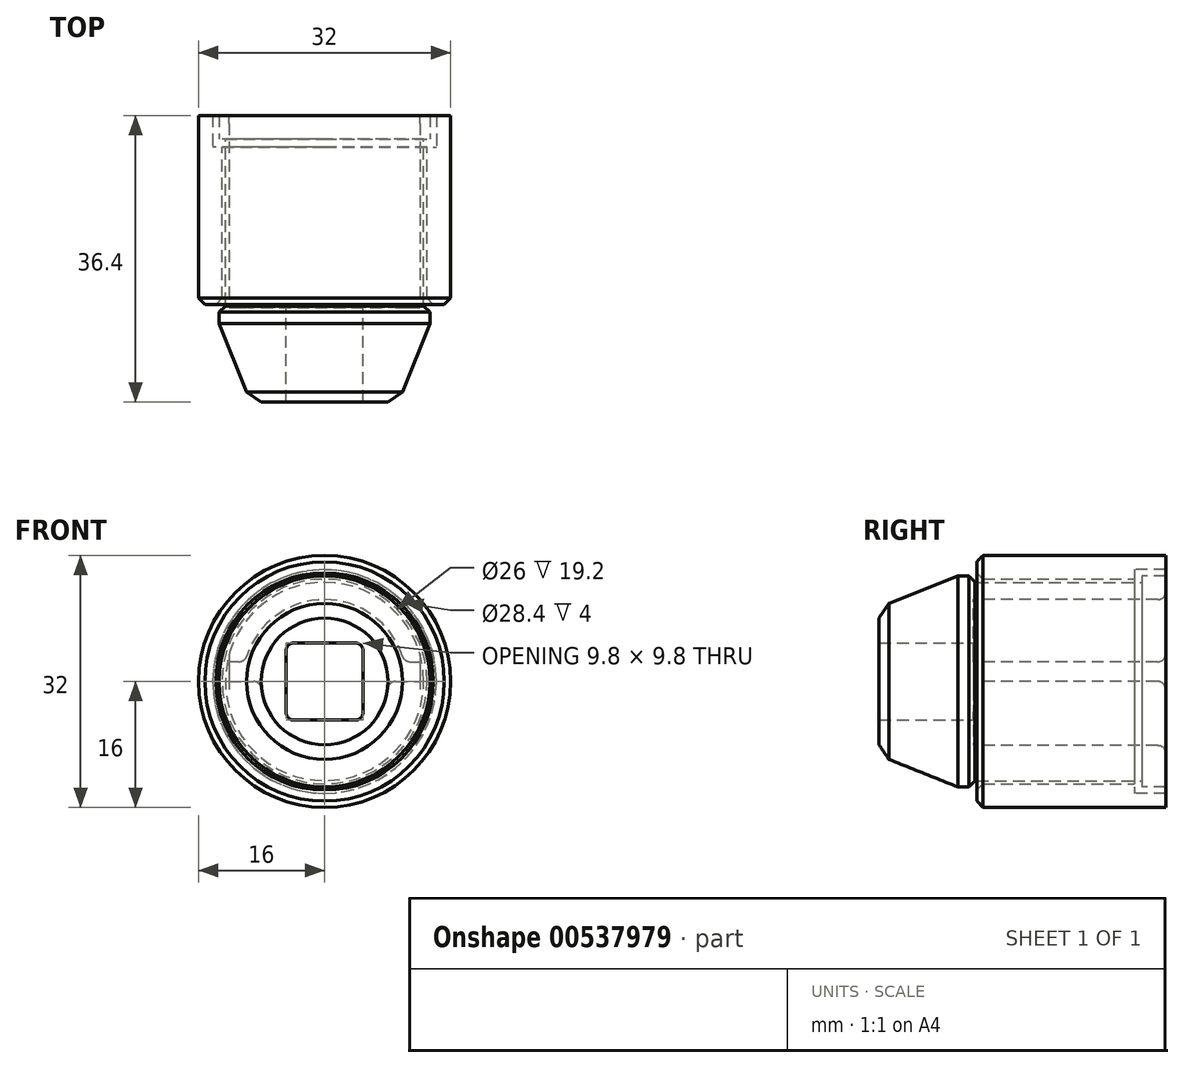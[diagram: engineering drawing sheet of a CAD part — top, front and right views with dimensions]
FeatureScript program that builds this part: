
annotation { "Feature Type Name" : "Feature", "Feature Type Description" : "" }
export const myFeature = defineFeature(function(context is Context, id is Id, definition is map)
    precondition{}
    {
        {
            var Q0;
            Q0=qCreatedBy(makeId("Front.planeOp"),FACE);
            var sketch = newSketch(context, id + "F0", { "sketchPlane" : qUnion([Q0])});
            skCircle(sketch, "E0", {"center": v(0, 0) * mm, "radius": 10.4 * mm});
            skCircle(sketch, "E1", {"center": v(0, 0) * mm, "radius": 13.4 * mm});
            skLineSegment(sketch, "E2", {"start": v(-13.4, 0) * mm, "end": v(13.4, 0) * mm});
            skCircle(sketch, "E3", {"center": v(0, 0) * mm, "radius": 8.1 * mm});
            skLineSegment(sketch, "E4.bottom", {"start": v(4.9, 4.9) * mm, "end": v(-4.9, 4.9) * mm});
            skLineSegment(sketch, "E4.top", {"start": v(4.9, -4.9) * mm, "end": v(-4.9, -4.9) * mm});
            skLineSegment(sketch, "E4.left", {"start": v(4.9, 4.9) * mm, "end": v(4.9, -4.9) * mm});
            skLineSegment(sketch, "E4.right", {"start": v(-4.9, 4.9) * mm, "end": v(-4.9, -4.9) * mm});
            skLineSegment(sketch, "E5", {"start": v(-10.1, 2.5) * mm, "end": v(-12.1, 2.5) * mm});
            skLineSegment(sketch, "E6", {"start": v(-12.1, 2.5) * mm, "end": v(-12.1, -2.5) * mm});
            skLineSegment(sketch, "E7", {"start": v(-12.1, -2.5) * mm, "end": v(-10.1, -2.5) * mm});
            skLineSegment(sketch, "E8.MirrorCS", {"start": v(10.1, 2.5) * mm, "end": v(12.1, 2.5) * mm});
            skLineSegment(sketch, "E9.MirrorCS", {"start": v(12.1, 2.5) * mm, "end": v(12.1, -2.5) * mm});
            skLineSegment(sketch, "E10.MirrorCS", {"start": v(12.1, -2.5) * mm, "end": v(10.1, -2.5) * mm});
            skSolve(sketch);
        }
        {
            var Q0;
            {var subQ5=sQuery(id+"F0.wireOp",EDGE,"E7");Q0=makeQuery(id+"F0.imprint","IMPRINT",FACE,{"disambiguationData":[TD([[makeQuery(id+"F0.imprint","IMPRINT",EDGE,{"derivedFrom":subQ5}),-1.0]])]});}
            var Q1;
            {var subQ9=sQuery(id+"F0.wireOp",EDGE,"E5");Q1=makeQuery(id+"F0.imprint","IMPRINT",FACE,{"disambiguationData":[TD([[makeQuery(id+"F0.imprint","IMPRINT",EDGE,{"derivedFrom":subQ9}),-1.0]])]});}
            extrude(context, id + "F1", {"entities" : qUnion([Q0, Q1]), "oppositeDirection" : true, "depth" : 24.4 * mm, "offsetDistance" : 25 * mm});
        }
        {
            var Q0;
            {var subQ0=sQuery(id+"F0.wireOp",EDGE,"E4.bottom");Q0=makeQuery(id+"F0.imprint","IMPRINT",FACE,{"disambiguationData":[TD([[makeQuery(id+"F0.imprint","IMPRINT",EDGE,{"derivedFrom":subQ0}),-1.0]])]});}
            var Q1;
            {var subQ0=sQuery(id+"F0.wireOp",EDGE,"E0");var subQ4=makeQuery(id+"F0.imprint","INTERSECT",VERTEX,{"derivedFrom":[subQ0,sQuery(id+"F0.wireOp",EDGE,"E8.MirrorCS")]});Q1=makeQuery(id+"F0.imprint","IMPRINT",FACE,{"disambiguationData":[TD([[makeQuery(id+"F0.imprint","IMPRINT",EDGE,{"disambiguationData":[TD([[subQ4,1.0]])],"derivedFrom":subQ0}),1.0]])]});}
            var Q2;
            {var subQ9=sQuery(id+"F0.wireOp",EDGE,"E5");Q2=makeQuery(id+"F0.imprint","IMPRINT",FACE,{"disambiguationData":[TD([[makeQuery(id+"F0.imprint","IMPRINT",EDGE,{"derivedFrom":subQ9}),-1.0]])]});}
            var Q3;
            {var subQ0=sQuery(id+"F0.wireOp",EDGE,"E4.top");Q3=makeQuery(id+"F0.imprint","IMPRINT",FACE,{"disambiguationData":[TD([[makeQuery(id+"F0.imprint","IMPRINT",EDGE,{"derivedFrom":subQ0}),1.0]])]});}
            var Q4;
            {var subQ1=sQuery(id+"F0.wireOp",EDGE,"E0");var subQ7=makeQuery(id+"F0.imprint","INTERSECT",VERTEX,{"derivedFrom":[subQ1,sQuery(id+"F0.wireOp",EDGE,"E7")]});Q4=makeQuery(id+"F0.imprint","IMPRINT",FACE,{"disambiguationData":[TD([[makeQuery(id+"F0.imprint","IMPRINT",EDGE,{"disambiguationData":[TD([[subQ7,1.0]])],"derivedFrom":subQ1}),1.0]])]});}
            var Q5;
            {var subQ5=sQuery(id+"F0.wireOp",EDGE,"E7");Q5=makeQuery(id+"F0.imprint","IMPRINT",FACE,{"disambiguationData":[TD([[makeQuery(id+"F0.imprint","IMPRINT",EDGE,{"derivedFrom":subQ5}),-1.0]])]});}
            var Q6;
            {var subQ0=sQuery(id+"F0.wireOp",EDGE,"E10.MirrorCS");Q6=makeQuery(id+"F0.imprint","IMPRINT",FACE,{"disambiguationData":[TD([[makeQuery(id+"F0.imprint","IMPRINT",EDGE,{"derivedFrom":subQ0}),-1.0]])]});}
            var Q7;
            {var subQ0=sQuery(id+"F0.wireOp",EDGE,"E8.MirrorCS");Q7=makeQuery(id+"F0.imprint","IMPRINT",FACE,{"disambiguationData":[TD([[makeQuery(id+"F0.imprint","IMPRINT",EDGE,{"derivedFrom":subQ0}),-1.0]])]});}
            var Q8;
            {var subQ0=sQuery(id+"F0.wireOp",EDGE,"E7");Q8=makeQuery(id+"F0.imprint","IMPRINT",FACE,{"disambiguationData":[TD([[makeQuery(id+"F0.imprint","IMPRINT",EDGE,{"derivedFrom":subQ0}),1.0]])]});}
            var Q9;
            {var subQ0=sQuery(id+"F0.wireOp",EDGE,"E5");Q9=makeQuery(id+"F0.imprint","IMPRINT",FACE,{"disambiguationData":[TD([[makeQuery(id+"F0.imprint","IMPRINT",EDGE,{"derivedFrom":subQ0}),1.0]])]});}
            extrude(context, id + "F2", {"entities" : qUnion([Q0, Q1, Q2, Q3, Q4, Q5, Q6, Q7, Q8, Q9]), "operationType" : NewBodyOperationType.ADD, "depth" : 12 * mm, "offsetDistance" : 25 * mm});
        }
        {
            var Q0;
            Q0=makeQuery(id+"F2.opExtrude","SWEPT_EDGE",EDGE,{"disambiguationData":[OSD([sQuery(id+"F0.wireOp",EDGE,"E4.bottom"),sQuery(id+"F0.wireOp",EDGE,"E4.right")])]});
            var Q1;
            Q1=makeQuery(id+"F2.opExtrude","SWEPT_EDGE",EDGE,{"disambiguationData":[OSD([sQuery(id+"F0.wireOp",EDGE,"E4.bottom"),sQuery(id+"F0.wireOp",EDGE,"E4.left")])]});
            var Q2;
            Q2=makeQuery(id+"F2.opExtrude","SWEPT_EDGE",EDGE,{"disambiguationData":[OSD([sQuery(id+"F0.wireOp",EDGE,"E4.top"),sQuery(id+"F0.wireOp",EDGE,"E4.left")])]});
            var Q3;
            Q3=makeQuery(id+"F2.opExtrude","SWEPT_EDGE",EDGE,{"disambiguationData":[OSD([sQuery(id+"F0.wireOp",EDGE,"E4.top"),sQuery(id+"F0.wireOp",EDGE,"E4.right")])]});
            fillet(context, id + "F3", {"entities" : qUnion([Q0, Q1, Q2, Q3]), "radius" : 1 * mm, "tangentPropagation" : true, "allowEdgeOverflow" : false});
        }
        {
            var Q0;
            {var subQ0=sQuery(id+"F0.wireOp",EDGE,"E10.MirrorCS");Q0=makeQuery(id+"F0.imprint","IMPRINT",FACE,{"disambiguationData":[TD([[makeQuery(id+"F0.imprint","IMPRINT",EDGE,{"derivedFrom":subQ0}),-1.0]])]});}
            var Q1;
            {var subQ1=sQuery(id+"F0.wireOp",EDGE,"E0");var subQ7=makeQuery(id+"F0.imprint","INTERSECT",VERTEX,{"derivedFrom":[subQ1,sQuery(id+"F0.wireOp",EDGE,"E7")]});Q1=makeQuery(id+"F0.imprint","IMPRINT",FACE,{"disambiguationData":[TD([[makeQuery(id+"F0.imprint","IMPRINT",EDGE,{"disambiguationData":[TD([[subQ7,1.0]])],"derivedFrom":subQ1}),1.0]])]});}
            var Q2;
            {var subQ0=sQuery(id+"F0.wireOp",EDGE,"E7");Q2=makeQuery(id+"F0.imprint","IMPRINT",FACE,{"disambiguationData":[TD([[makeQuery(id+"F0.imprint","IMPRINT",EDGE,{"derivedFrom":subQ0}),1.0]])]});}
            var Q3;
            Q3=makeQuery(id+"F1.opExtrude","CAP_FACE",FACE,{"disambiguationData":[OSD([sQuery(id+"F0.wireOp",EDGE,"E0"),sQuery(id+"F0.wireOp",EDGE,"E1"),sQuery(id+"F0.wireOp",EDGE,"E5"),sQuery(id+"F0.wireOp",EDGE,"E6"),sQuery(id+"F0.wireOp",EDGE,"E7"),sQuery(id+"F0.wireOp",EDGE,"E8.MirrorCS"),sQuery(id+"F0.wireOp",EDGE,"E9.MirrorCS"),sQuery(id+"F0.wireOp",EDGE,"E10.MirrorCS")])],"isStart":false});
            extrude(context, id + "F4", {"entities" : qUnion([Q0, Q1, Q2]), "operationType" : NewBodyOperationType.ADD, "endBound" : BoundingType.UP_TO_SURFACE, "oppositeDirection" : true, "depth" : 25 * mm, "endBoundEntityFace" : qUnion([Q3]), "offsetDistance" : 25 * mm});
        }
        {
            var Q0;
            Q0=makeQuery(id+"F2.opExtrude","CAP_EDGE",EDGE,{"disambiguationData":[OSD([sQuery(id+"F0.wireOp",EDGE,"E1")])],"isStart":false});
            chamfer(context, id + "F5", {"entities" : qUnion([Q0]), "chamferType" : ChamferType.TWO_OFFSETS, "width1" : 10 * mm, "oppositeDirection" : true, "width2" : 4 * mm, "tangentPropagation" : true});
        }
        {
            var Q0;
            {var subQ0=sQuery(id+"F0.wireOp",EDGE,"E10.MirrorCS");var subQ1=sQuery(id+"F0.wireOp",EDGE,"E9.MirrorCS");var subQ2=sQuery(id+"F0.wireOp",EDGE,"E7");var subQ3=sQuery(id+"F0.wireOp",EDGE,"E6");var subQ4=sQuery(id+"F0.wireOp",EDGE,"E0");Q0=makeQuery(id+"F4.boolean.opBoolean","MERGE",FACE,{"derivedFrom":[makeQuery(id+"F1.opExtrude","CAP_FACE",FACE,{"disambiguationData":[OSD([subQ4,sQuery(id+"F0.wireOp",EDGE,"E1"),sQuery(id+"F0.wireOp",EDGE,"E5"),subQ3,subQ2,sQuery(id+"F0.wireOp",EDGE,"E8.MirrorCS"),subQ1,subQ0])],"isStart":false}),makeQuery(id+"F4.opExtrude","CAP_FACE",FACE,{"disambiguationData":[OSD([subQ4,sQuery(id+"F0.wireOp",EDGE,"E2"),sQuery(id+"F0.wireOp",EDGE,"E3"),subQ3,subQ2,subQ1,subQ0])],"isStart":false})]});}
            cPlane(context, id + "F6", {"entities" : qUnion([Q0]), "cplaneType" : CPlaneType.OFFSET, "offset" : 3 * mm, "oppositeDirection" : true, "width" : 150 * mm, "height" : 150 * mm});
        }
        {
            var Q0;
            Q0=qCreatedBy(id+"F6.planeOp",FACE);
            var sketch = newSketch(context, id + "F7", { "sketchPlane" : qUnion([Q0])});
            skCircle(sketch, "E11", {"center": v(0, 0) * mm, "radius": 12.6 * mm});
            skCircle(sketch, "E12", {"center": v(0, 0) * mm, "radius": 13.4 * mm});
            skSolve(sketch);
        }
        {
            var Q0;
            Q0=makeQuery(id+"F7.imprint","IMPRINT",FACE,{"disambiguationData":[TD([[makeQuery(id+"F7.imprint","IMPRINT",EDGE,{"derivedFrom":sQuery(id+"F7.wireOp",EDGE,"E11")}),-1.0]])]});
            extrude(context, id + "F8", {"entities" : qUnion([Q0]), "operationType" : NewBodyOperationType.REMOVE, "oppositeDirection" : true, "depth" : 22 * mm, "offsetDistance" : 25 * mm});
        }
        {
            var Q0;
            Q0=qCreatedBy(id+"F6.planeOp",FACE);
            cPlane(context, id + "F9", {"entities" : qUnion([Q0]), "cplaneType" : CPlaneType.OFFSET, "offset" : 1 * mm, "oppositeDirection" : true, "width" : 150 * mm, "height" : 150 * mm});
        }
        {
            var Q0;
            Q0=qCreatedBy(id+"F9.planeOp",FACE);
            var sketch = newSketch(context, id + "F10", { "sketchPlane" : qUnion([Q0])});
            skCircle(sketch, "E13", {"center": v(0, 0) * mm, "radius": 13 * mm});
            skCircle(sketch, "E14", {"center": v(0, 0) * mm, "radius": 16 * mm});
            skCircle(sketch, "E15", {"center": v(0, 0) * mm, "radius": 14.2 * mm});
            skSolve(sketch);
        }
        {
            var Q0;
            {var subQ0=sQuery(id+"F0.wireOp",EDGE,"E1");Q0=makeQuery(id+"F5.opChamfer","BLEND_EDGE",EDGE,{"blendedFrom":[makeQuery(id+"F2.opExtrude","CAP_EDGE",EDGE,{"disambiguationData":[OSD([subQ0])],"isStart":false}),makeQuery(id+"F2.opExtrude","CAP_FACE",FACE,{"disambiguationData":[OSD([subQ0,sQuery(id+"F0.wireOp",EDGE,"E4.bottom"),sQuery(id+"F0.wireOp",EDGE,"E4.top"),sQuery(id+"F0.wireOp",EDGE,"E4.left"),sQuery(id+"F0.wireOp",EDGE,"E4.right")])],"isStart":false})],"blendedInto":[makeQuery(id+"F2.opExtrude","CAP_FACE",FACE,{"disambiguationData":[OSD([subQ0,sQuery(id+"F0.wireOp",EDGE,"E4.bottom"),sQuery(id+"F0.wireOp",EDGE,"E4.top"),sQuery(id+"F0.wireOp",EDGE,"E4.left"),sQuery(id+"F0.wireOp",EDGE,"E4.right")])],"isStart":false})]});}
            chamfer(context, id + "F11", {"entities" : qUnion([Q0]), "width" : 2 * mm, "tangentPropagation" : true});
        }
        {
            var Q0;
            Q0=makeQuery(id+"F10.imprint","IMPRINT",FACE,{"disambiguationData":[TD([[makeQuery(id+"F10.imprint","IMPRINT",EDGE,{"derivedFrom":sQuery(id+"F10.wireOp",EDGE,"E13")}),-1.0]])]});
            var Q1;
            Q1=makeQuery(id+"F10.imprint","IMPRINT",FACE,{"disambiguationData":[TD([[makeQuery(id+"F10.imprint","IMPRINT",EDGE,{"derivedFrom":sQuery(id+"F10.wireOp",EDGE,"E14")}),1.0]])]});
            extrude(context, id + "F12", {"entities" : qUnion([Q0, Q1]), "oppositeDirection" : true, "depth" : 20 * mm, "offsetDistance" : 25 * mm});
        }
        {
            var Q0;
            Q0=makeQuery(id+"F10.imprint","IMPRINT",FACE,{"disambiguationData":[TD([[makeQuery(id+"F10.imprint","IMPRINT",EDGE,{"derivedFrom":sQuery(id+"F10.wireOp",EDGE,"E14")}),1.0]])]});
            var Q1;
            {var subQ0=sQuery(id+"F0.wireOp",EDGE,"E10.MirrorCS");var subQ1=sQuery(id+"F0.wireOp",EDGE,"E9.MirrorCS");var subQ2=sQuery(id+"F0.wireOp",EDGE,"E7");var subQ3=sQuery(id+"F0.wireOp",EDGE,"E6");var subQ4=sQuery(id+"F0.wireOp",EDGE,"E0");Q1=makeQuery(id+"F4.boolean.opBoolean","MERGE",FACE,{"derivedFrom":[makeQuery(id+"F1.opExtrude","CAP_FACE",FACE,{"disambiguationData":[OSD([subQ4,sQuery(id+"F0.wireOp",EDGE,"E1"),sQuery(id+"F0.wireOp",EDGE,"E5"),subQ3,subQ2,sQuery(id+"F0.wireOp",EDGE,"E8.MirrorCS"),subQ1,subQ0])],"isStart":false}),makeQuery(id+"F4.opExtrude","CAP_FACE",FACE,{"disambiguationData":[OSD([subQ4,sQuery(id+"F0.wireOp",EDGE,"E2"),sQuery(id+"F0.wireOp",EDGE,"E3"),subQ3,subQ2,subQ1,subQ0])],"isStart":false})]});}
            extrude(context, id + "F13", {"entities" : qUnion([Q0]), "operationType" : NewBodyOperationType.ADD, "endBound" : BoundingType.UP_TO_SURFACE, "depth" : 25 * mm, "endBoundEntityFace" : qUnion([Q1]), "offsetDistance" : 25 * mm});
        }
        {
            var Q0;
            Q0=makeQuery(id+"F8.boolean.opBoolean","COPY",EDGE,{"derivedFrom":makeQuery(id+"F8.opExtrude","CAP_EDGE",EDGE,{"disambiguationData":[OSD([sQuery(id+"F7.wireOp",EDGE,"E12")])],"isStart":true})});
            var Q1;
            Q1=makeQuery(id+"F12.opExtrude","CAP_EDGE",EDGE,{"disambiguationData":[OSD([sQuery(id+"F10.wireOp",EDGE,"E14")])],"isStart":false});
            var Q2;
            Q2=makeQuery(id+"F13.opExtrude","CAP_EDGE",EDGE,{"disambiguationData":[OSD([sQuery(id+"F10.wireOp",EDGE,"E15")])],"isStart":true});
            var Q3;
            Q3=makeQuery(id+"F12.opExtrude","CAP_EDGE",EDGE,{"disambiguationData":[OSD([sQuery(id+"F10.wireOp",EDGE,"E13")])],"isStart":false});
            var Q4;
            Q4=makeQuery(id+"F8.boolean.opBoolean","COPY",EDGE,{"derivedFrom":makeQuery(id+"F8.opExtrude","CAP_EDGE",EDGE,{"disambiguationData":[OSD([sQuery(id+"F7.wireOp",EDGE,"E11")])],"isStart":false})});
            chamfer(context, id + "F14", {"entities" : qUnion([Q0, Q1, Q2, Q3, Q4]), "width" : .8 * mm, "tangentPropagation" : true});
        }
        {
            var Q0;
            {var subQ0=sQuery(id+"F0.wireOp",EDGE,"E3");var subQ1=sQuery(id+"F0.wireOp",EDGE,"E2");Q0=makeQuery(id+"F4.opExtrude","SWEPT_EDGE",EDGE,{"disambiguationData":[OSD([subQ1,subQ0]),TDD([makeQuery(id+"F0.imprint","INTERSECT",VERTEX,{"disambiguationData":[OD(1.0)],"derivedFrom":[subQ1,subQ0]})])]});}
            var Q1;
            {var subQ0=sQuery(id+"F0.wireOp",EDGE,"E3");var subQ1=sQuery(id+"F0.wireOp",EDGE,"E2");var subQ2=makeQuery(id+"F0.imprint","INTERSECT",VERTEX,{"disambiguationData":[OD(0.0)],"derivedFrom":[sQuery(id+"F0.wireOp",EDGE,"E0"),subQ1]});Q1=makeQuery(id+"F8MjM1Ex5uowhJ1_2.opChamfer","BLEND_EDGE",EDGE,{"blendedFrom":[makeQuery(id+"F4.opExtrude","CAP_EDGE",EDGE,{"disambiguationData":[OSD([subQ1]),TDD([makeQuery(id+"F0.imprint","IMPRINT",EDGE,{"disambiguationData":[TD([[subQ2,1.0]])],"derivedFrom":subQ1}),makeQuery(id+"F0.imprint","IMPRINT",EDGE,{"disambiguationData":[TD([[subQ2,-1.0]])],"derivedFrom":subQ1})])],"isStart":false}),makeQuery(id+"F4.opExtrude","CAP_EDGE",EDGE,{"disambiguationData":[OSD([subQ0])],"isStart":false})],"blendedInto":[]});}
            var Q2;
            {var subQ0=sQuery(id+"F0.wireOp",EDGE,"E3");var subQ1=sQuery(id+"F0.wireOp",EDGE,"E2");Q2=makeQuery(id+"F4.opExtrude","SWEPT_EDGE",EDGE,{"disambiguationData":[OSD([subQ1,subQ0]),TDD([makeQuery(id+"F0.imprint","INTERSECT",VERTEX,{"disambiguationData":[OD(0.0)],"derivedFrom":[subQ1,subQ0]})])]});}
            var Q3;
            {var subQ0=sQuery(id+"F0.wireOp",EDGE,"E3");var subQ1=sQuery(id+"F0.wireOp",EDGE,"E2");var subQ2=makeQuery(id+"F0.imprint","INTERSECT",VERTEX,{"disambiguationData":[OD(1.0)],"derivedFrom":[sQuery(id+"F0.wireOp",EDGE,"E0"),subQ1]});Q3=makeQuery(id+"F8MjM1Ex5uowhJ1_2.opChamfer","BLEND_EDGE",EDGE,{"blendedFrom":[makeQuery(id+"F4.opExtrude","CAP_EDGE",EDGE,{"disambiguationData":[OSD([subQ1]),TDD([makeQuery(id+"F0.imprint","IMPRINT",EDGE,{"disambiguationData":[TD([[subQ2,1.0]])],"derivedFrom":subQ1}),makeQuery(id+"F0.imprint","IMPRINT",EDGE,{"disambiguationData":[TD([[subQ2,-1.0]])],"derivedFrom":subQ1})])],"isStart":false}),makeQuery(id+"F4.opExtrude","CAP_EDGE",EDGE,{"disambiguationData":[OSD([subQ0])],"isStart":false})],"blendedInto":[]});}
            fillet(context, id + "F15", {"entities" : qUnion([Q0, Q1, Q2, Q3]), "radius" : 1 * mm, "tangentPropagation" : true, "allowEdgeOverflow" : false});
        }
        {
            var Q0;
            Q0=makeQuery(id+"F1.opExtrude","SWEPT_EDGE",EDGE,{"disambiguationData":[OSD([sQuery(id+"F0.wireOp",EDGE,"E0"),sQuery(id+"F0.wireOp",EDGE,"E8.MirrorCS")])]});
            var Q1;
            {var subQ0=sQuery(id+"F0.wireOp",EDGE,"E0");Q1=makeQuery(id+"F1.opExtrude","CAP_EDGE",EDGE,{"disambiguationData":[OSD([subQ0]),TDD([makeQuery(id+"F0.imprint","IMPRINT",EDGE,{"disambiguationData":[TD([[makeQuery(id+"F0.imprint","INTERSECT",VERTEX,{"derivedFrom":[subQ0,sQuery(id+"F0.wireOp",EDGE,"E5")]}),1.0]])],"derivedFrom":subQ0})])],"isStart":false});}
            var Q2;
            Q2=makeQuery(id+"F1.opExtrude","SWEPT_EDGE",EDGE,{"disambiguationData":[OSD([sQuery(id+"F0.wireOp",EDGE,"E0"),sQuery(id+"F0.wireOp",EDGE,"E5")])]});
            var Q3;
            Q3=makeQuery(id+"F1.opExtrude","CAP_EDGE",EDGE,{"disambiguationData":[OSD([sQuery(id+"F0.wireOp",EDGE,"E5")])],"isStart":false});
            var Q4;
            Q4=makeQuery(id+"F1.opExtrude","CAP_EDGE",EDGE,{"disambiguationData":[OSD([sQuery(id+"F0.wireOp",EDGE,"E8.MirrorCS")])],"isStart":false});
            var Q5;
            {var subQ0=sQuery(id+"F0.wireOp",EDGE,"E2");var subQ1=makeQuery(id+"F0.imprint","INTERSECT",VERTEX,{"disambiguationData":[OD(1.0)],"derivedFrom":[sQuery(id+"F0.wireOp",EDGE,"E0"),subQ0]});Q5=makeQuery(id+"F4.opExtrude","CAP_EDGE",EDGE,{"disambiguationData":[OSD([subQ0]),TDD([makeQuery(id+"F0.imprint","IMPRINT",EDGE,{"disambiguationData":[TD([[subQ1,1.0]])],"derivedFrom":subQ0}),makeQuery(id+"F0.imprint","IMPRINT",EDGE,{"disambiguationData":[TD([[subQ1,-1.0]])],"derivedFrom":subQ0})])],"isStart":false});}
            fillet(context, id + "F16", {"entities" : qUnion([Q0, Q1, Q2, Q3, Q4, Q5]), "radius" : 1 * mm, "tangentPropagation" : true, "defaultsChanged" : false, "vertexSettings" : [], "allowEdgeOverflow" : false});
        }
    });
